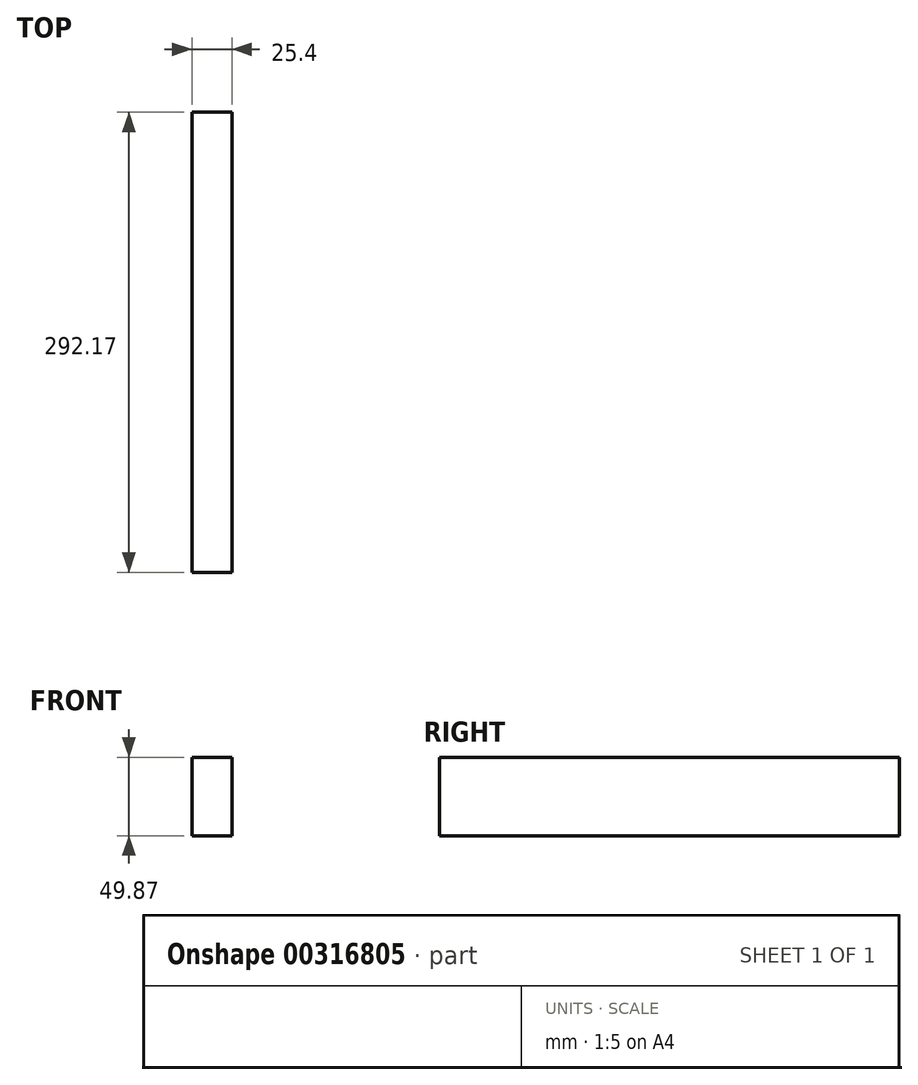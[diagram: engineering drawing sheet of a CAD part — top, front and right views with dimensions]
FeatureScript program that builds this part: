
annotation { "Feature Type Name" : "Feature", "Feature Type Description" : "" }
export const myFeature = defineFeature(function(context is Context, id is Id, definition is map)
    precondition{}
    {
        {
            var Q0;
            Q0=qCreatedBy(makeId("Right.planeOp"),FACE);
            var sketch = newSketch(context, id + "F0", { "sketchPlane" : qUnion([Q0])});
            skLineSegment(sketch, "E0.bottom", {"start": v(-220.88, 35.41) * mm, "end": v(71.3, 35.41) * mm});
            skLineSegment(sketch, "E0.top", {"start": v(-220.88, -14.46) * mm, "end": v(71.3, -14.46) * mm});
            skLineSegment(sketch, "E0.left", {"start": v(-220.88, 35.41) * mm, "end": v(-220.88, -14.46) * mm});
            skLineSegment(sketch, "E0.right", {"start": v(71.3, 35.41) * mm, "end": v(71.3, -14.46) * mm});
            skPoint(sketch, "E1.oppositeSnap0", {"position": v(-220.88, 10.47) * mm});
            skLineSegment(sketch, "E1.bottom", {"start": v(-220.88, 10.47) * mm, "end": v(-73.26, 10.47) * mm});
            skLineSegment(sketch, "E1.top", {"start": v(-220.88, 10.47) * mm, "end": v(-73.26, 10.47) * mm});
            skLineSegment(sketch, "E1.left", {"start": v(-220.88, 10.47) * mm, "end": v(-220.88, 10.47) * mm});
            skLineSegment(sketch, "E1.right", {"start": v(-73.26, 10.47) * mm, "end": v(-73.26, 10.47) * mm});
            skSolve(sketch);
        }
        {
            var Q0;
            Q0 = qSketchRegion(id + "F0", true);
            var Q1;
            {var subQ3=sQuery(id+"F0.wireOp",EDGE,"E0.bottom");Q1=makeQuery(id+"F0.imprint","IMPRINT",FACE,{"disambiguationData":[TD([[makeQuery(id+"F0.imprint","IMPRINT",EDGE,{"derivedFrom":subQ3}),-1.0]])]});}
            extrude(context, id + "F1", {"entities" : qUnion([Q0, Q1]), "depth" : 25.4 * mm});
        }
    });
